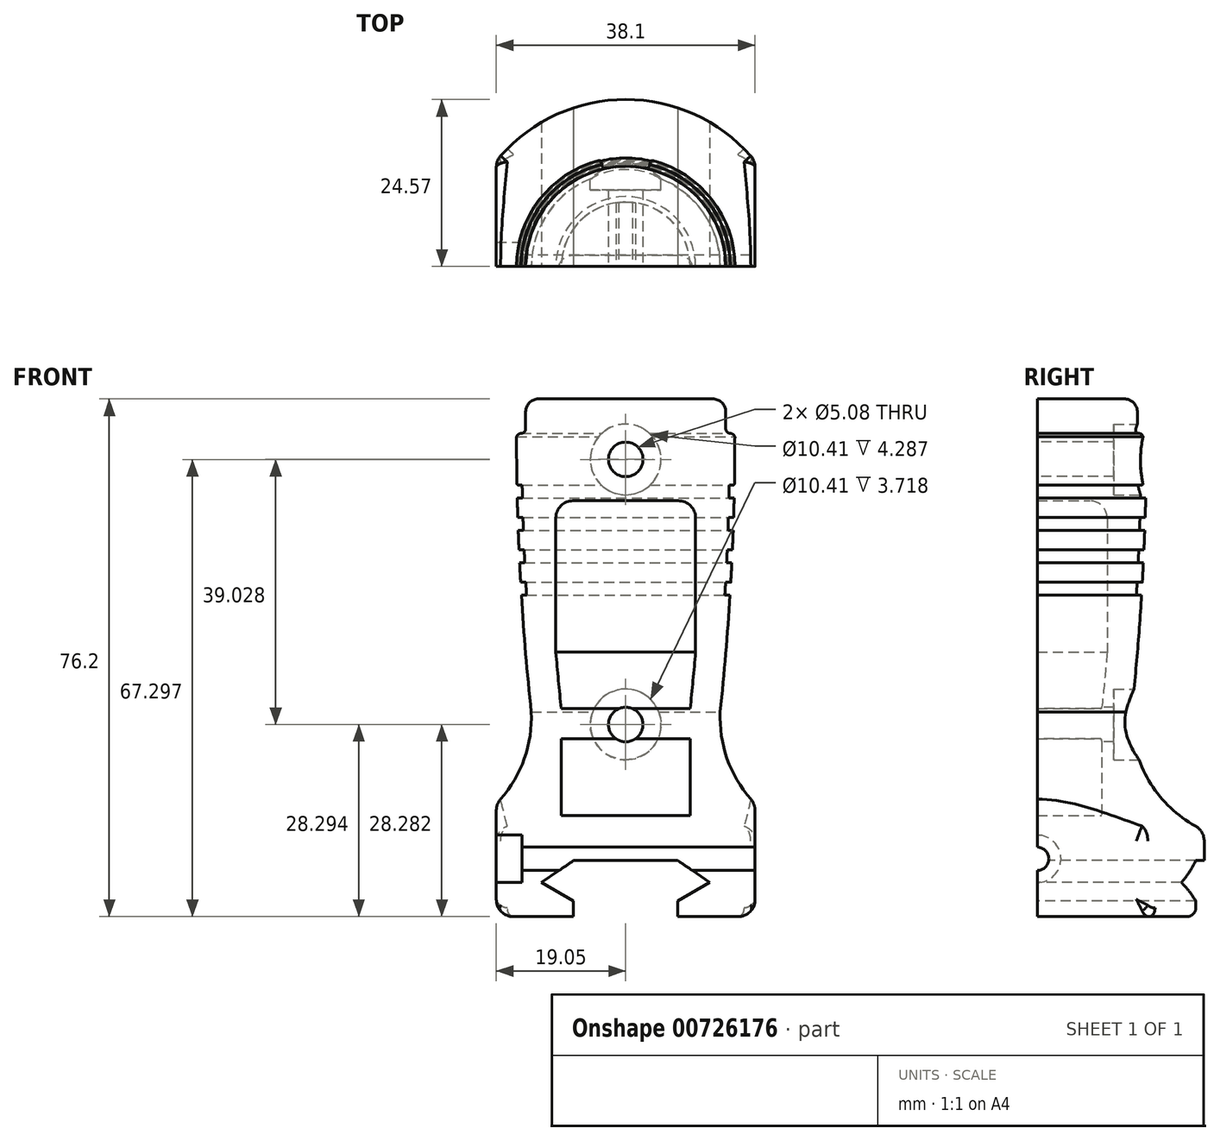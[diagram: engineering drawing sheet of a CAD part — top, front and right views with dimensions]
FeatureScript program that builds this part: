
annotation { "Feature Type Name" : "Feature", "Feature Type Description" : "" }
export const myFeature = defineFeature(function(context is Context, id is Id, definition is map)
    precondition{}
    {
        {
            var Q0;
            Q0=qCreatedBy(makeId("Front.planeOp"),FACE);
            var sketch = newSketch(context, id + "F0", { "sketchPlane" : qUnion([Q0])});
            skLineSegment(sketch, "E0", {"start": v(0, 76.2) * mm, "end": v(12.83, 76.2) * mm});
            skLineSegment(sketch, "E1.0", {"start": v(15.4, 71.12) * mm, "end": v(15.43, 71.12) * mm});
            skLineSegment(sketch, "E2.0", {"start": v(14.73, 71.82) * mm, "end": v(14.73, 74.3) * mm});
            skPoint(sketch, "E3.visualSharp", {"position": v(16.2, 71.12) * mm});
            skArc(sketch, "E3.filletArc", {"start": v(16.07, 70.62) * mm, "mid": v(15.82, 70.98) * mm, "end": v(15.4, 71.12) * mm});
            skPoint(sketch, "E4.visualSharp", {"position": v(14.73, 71.12) * mm});
            skArc(sketch, "E4.filletArc", {"start": v(14.73, 71.82) * mm, "mid": v(14.94, 71.32) * mm, "end": v(15.43, 71.12) * mm});
            skPoint(sketch, "E5.visualSharp", {"position": v(14.73, 76.2) * mm});
            skArc(sketch, "E5.filletArc", {"start": v(14.73, 74.3) * mm, "mid": v(14.17, 75.64) * mm, "end": v(12.83, 76.2) * mm});
            skArc(sketch, "E6", {"start": v(13.9, 30.14) * mm, "mid": v(14.73, 38.71) * mm, "end": v(15.36, 47.3) * mm});
            skPoint(sketch, "E7.orphan", {"position": v(16.2, 0) * mm});
            skLineSegment(sketch, "E8.0", {"start": v(15.24, 63.5) * mm, "end": v(15.76, 63.5) * mm});
            skLineSegment(sketch, "E9.0", {"start": v(15.2, 61.6) * mm, "end": v(15.97, 61.6) * mm});
            skLineSegment(sketch, "E10.0", {"start": v(15.12, 58.74) * mm, "end": v(15.89, 58.74) * mm});
            skLineSegment(sketch, "E11.0", {"start": v(15.06, 56.83) * mm, "end": v(15.82, 56.83) * mm});
            skLineSegment(sketch, "E12.0", {"start": v(14.94, 53.98) * mm, "end": v(15.7, 53.98) * mm});
            skLineSegment(sketch, "E13.0", {"start": v(14.86, 52.07) * mm, "end": v(15.62, 52.07) * mm});
            skLineSegment(sketch, "E14.0", {"start": v(14.7, 49.21) * mm, "end": v(15.47, 49.21) * mm});
            skLineSegment(sketch, "E15.0", {"start": v(14.6, 47.3) * mm, "end": v(15.36, 47.3) * mm});
            skArc(sketch, "E16.0", {"start": v(14.6, 47.3) * mm, "mid": v(14.65, 48.26) * mm, "end": v(14.7, 49.21) * mm});
            skArc(sketch, "E17.trimOffspring", {"start": v(16.01, 63.75) * mm, "mid": v(16.06, 67.18) * mm, "end": v(16.07, 70.62) * mm});
            skArc(sketch, "E18.trimOffspring", {"start": v(15.2, 61.6) * mm, "mid": v(15.22, 62.55) * mm, "end": v(15.24, 63.5) * mm});
            skArc(sketch, "E19.trimOffspring", {"start": v(15.89, 58.74) * mm, "mid": v(15.93, 60.17) * mm, "end": v(15.97, 61.6) * mm});
            skArc(sketch, "E20.trimOffspring", {"start": v(15.06, 56.83) * mm, "mid": v(15.1, 57.78) * mm, "end": v(15.12, 58.74) * mm});
            skArc(sketch, "E21.trimOffspring", {"start": v(15.7, 53.98) * mm, "mid": v(15.77, 55.4) * mm, "end": v(15.82, 56.83) * mm});
            skArc(sketch, "E22.trimOffspring", {"start": v(14.86, 52.07) * mm, "mid": v(14.9, 53.02) * mm, "end": v(14.94, 53.98) * mm});
            skArc(sketch, "E23.trimOffspring", {"start": v(15.47, 49.21) * mm, "mid": v(15.55, 50.64) * mm, "end": v(15.62, 52.07) * mm});
            skPoint(sketch, "E24.visualSharp", {"position": v(16, 63.5) * mm});
            skArc(sketch, "E24.filletArc", {"start": v(15.76, 63.5) * mm, "mid": v(15.93, 63.57) * mm, "end": v(16.01, 63.75) * mm});
            skLineSegment(sketch, "E25", {"start": v(0, 0) * mm, "end": v(23.3, 0) * mm});
            skLineSegment(sketch, "E26", {"start": v(24.57, 1.27) * mm, "end": v(24.57, 11.14) * mm});
            skArc(sketch, "E27", {"start": v(13.9, 30.14) * mm, "mid": v(16.2, 20.42) * mm, "end": v(23.27, 13.36) * mm});
            skPoint(sketch, "E28.visualSharp", {"position": v(24.57, 12.7) * mm});
            skArc(sketch, "E28.filletArc", {"start": v(24.57, 11.14) * mm, "mid": v(24.22, 12.43) * mm, "end": v(23.27, 13.36) * mm});
            skPoint(sketch, "E29.visualSharp", {"position": v(24.57, 0) * mm});
            skArc(sketch, "E29.filletArc", {"start": v(23.3, 0) * mm, "mid": v(24.2, 0.37) * mm, "end": v(24.57, 1.27) * mm});
            skLineSegment(sketch, "E30.0", {"start": v(10.29, 38.93) * mm, "end": v(10.29, 58.67) * mm});
            skArc(sketch, "E31.0", {"start": v(9.49, 30.6) * mm, "mid": v(9.91, 34.77) * mm, "end": v(10.29, 38.93) * mm});
            skLineSegment(sketch, "E32", {"start": v(9.49, 30.6) * mm, "end": v(0, 30.6) * mm});
            skLineSegment(sketch, "E33.0", {"start": v(9.49, 26.16) * mm, "end": v(0, 26.16) * mm});
            skLineSegment(sketch, "E34", {"start": v(9.49, 26.16) * mm, "end": v(9.49, 14.86) * mm});
            skLineSegment(sketch, "E35", {"start": v(9.49, 14.86) * mm, "end": v(0, 14.86) * mm});
            skLineSegment(sketch, "E36.trimOffspring", {"start": v(0, 26.16) * mm, "end": v(0, 30.6) * mm});
            skLineSegment(sketch, "E37.trimOffspring", {"start": v(0, 61.21) * mm, "end": v(0, 76.2) * mm});
            skLineSegment(sketch, "E38", {"start": v(0, 14.86) * mm, "end": v(0, 0) * mm});
            skLineSegment(sketch, "E39.0", {"start": v(0, 61.21) * mm, "end": v(7.75, 61.21) * mm});
            skPoint(sketch, "E40.visualSharp", {"position": v(10.29, 61.21) * mm});
            skArc(sketch, "E40.filletArc", {"start": v(10.29, 58.67) * mm, "mid": v(9.54, 60.47) * mm, "end": v(7.75, 61.21) * mm});
            skSolve(sketch);
        }
        {
            var Q0;
            Q0=makeQuery(id+"F0.imprint","IMPRINT",FACE,{"disambiguationData":[TD([[makeQuery(id+"F0.imprint","IMPRINT",EDGE,{"derivedFrom":sQuery(id+"F0.wireOp",EDGE,"E0")}),-1.0]])]});
            var Q1;
            Q1=sQuery(id+"F0.wireOp",EDGE,"E37.trimOffspring");
            revolve(context, id + "F1", {"surfaceOperationType" : NewSurfaceOperationType.NEW, "entities" : qUnion([Q0]), "axis" : qUnion([Q1]), "revolveType" : RevolveType.FULL});
        }
        {
            var Q0;
            Q0=qCreatedBy(makeId("Front.planeOp"),FACE);
            var sketch = newSketch(context, id + "F2", { "sketchPlane" : qUnion([Q0])});
            skLineSegment(sketch, "E41.0", {"start": v(19.05, 0) * mm, "end": v(19.05, 22.93) * mm});
            skLineSegment(sketch, "E42.0", {"start": v(-19.05, 0) * mm, "end": v(-19.05, 22.93) * mm});
            skLineSegment(sketch, "E43", {"start": v(0, 0) * mm, "end": v(0, 22.93) * mm});
            skLineSegment(sketch, "E44.0", {"start": v(7.68, 0) * mm, "end": v(7.68, 2.29) * mm});
            skLineSegment(sketch, "E45", {"start": v(7.68, 0) * mm, "end": v(19.05, 0) * mm});
            skLineSegment(sketch, "E46.0", {"start": v(0, 8.26) * mm, "end": v(7.68, 8.26) * mm});
            skLineSegment(sketch, "E47", {"start": v(7.68, 2.29) * mm, "end": v(12.38, 5.02) * mm});
            skLineSegment(sketch, "E48", {"start": v(12.38, 5.02) * mm, "end": v(7.68, 8.26) * mm});
            skLineSegment(sketch, "E49.MirrorCS", {"start": v(0, 8.26) * mm, "end": v(-7.68, 8.26) * mm});
            skLineSegment(sketch, "E50.MirrorCS", {"start": v(-12.38, 5.02) * mm, "end": v(-7.68, 8.26) * mm});
            skLineSegment(sketch, "E51.MirrorCS", {"start": v(-7.68, 2.29) * mm, "end": v(-12.38, 5.02) * mm});
            skLineSegment(sketch, "E52.MirrorCS", {"start": v(-7.68, 0) * mm, "end": v(-7.68, 2.29) * mm});
            skPoint(sketch, "E53.orphan", {"position": v(7.68, 5.02) * mm});
            skPoint(sketch, "E54.orphan", {"position": v(-7.68, 5.02) * mm});
            skLineSegment(sketch, "E55", {"start": v(-7.68, 0) * mm, "end": v(-19.05, 0) * mm});
            skLineSegment(sketch, "E56", {"start": v(-19.05, 22.93) * mm, "end": v(-34.37, 22.93) * mm});
            skLineSegment(sketch, "E57", {"start": v(-34.37, 22.93) * mm, "end": v(-34.37, -12.19) * mm});
            skLineSegment(sketch, "E58", {"start": v(-34.37, -12.19) * mm, "end": v(36.04, -12.19) * mm});
            skLineSegment(sketch, "E59", {"start": v(36.04, -12.19) * mm, "end": v(36.04, 22.93) * mm});
            skLineSegment(sketch, "E60", {"start": v(36.04, 22.93) * mm, "end": v(19.05, 22.93) * mm});
            skSolve(sketch);
        }
        {
            var Q0;
            Q0=makeQuery(id+"F2.imprint","IMPRINT",FACE,{"disambiguationData":[TD([[makeQuery(id+"F2.imprint","IMPRINT",EDGE,{"derivedFrom":sQuery(id+"F2.wireOp",EDGE,"E41.0")}),-1.0]])]});
            extrude(context, id + "F3", {"entities" : qUnion([Q0]), "operationType" : NewBodyOperationType.REMOVE, "endBound" : BoundingType.SYMMETRIC, "oppositeDirection" : true, "depth" : 50.8 * mm, "offsetDistance" : 25.4 * mm});
        }
        {
            var Q0;
            Q0=makeQuery(id+"F3.boolean.opBoolean","INTERSECT",EDGE,{"derivedFrom":[makeQuery(id+"F1.opRevolve","SWEPT_FACE",FACE,{"disambiguationData":[OSD([sQuery(id+"F0.wireOp",EDGE,"E27")])]}),makeQuery(id+"F3.opExtrude","SWEPT_FACE",FACE,{"disambiguationData":[OSD([sQuery(id+"F2.wireOp",EDGE,"E41.0")])]})]});
            var Q1;
            Q1=makeQuery(id+"F3.boolean.opBoolean","INTERSECT",EDGE,{"derivedFrom":[makeQuery(id+"F1.opRevolve","SWEPT_FACE",FACE,{"disambiguationData":[OSD([sQuery(id+"F0.wireOp",EDGE,"E27")])]}),makeQuery(id+"F3.opExtrude","SWEPT_FACE",FACE,{"disambiguationData":[OSD([sQuery(id+"F2.wireOp",EDGE,"E42.0")])]})]});
            var Q2;
            Q2=makeQuery(id+"F3.boolean.opBoolean","INTERSECT",EDGE,{"disambiguationData":[OD(0.0)],"derivedFrom":[makeQuery(id+"F1.opRevolve","SWEPT_FACE",FACE,{"disambiguationData":[OSD([sQuery(id+"F0.wireOp",EDGE,"E26")])]}),makeQuery(id+"F3.opExtrude","SWEPT_FACE",FACE,{"disambiguationData":[OSD([sQuery(id+"F2.wireOp",EDGE,"E42.0")])]})]});
            fillet(context, id + "F4", {"entities" : qUnion([Q0, Q1, Q2]), "radius" : 2.54 * mm, "tangentPropagation" : true, "allowEdgeOverflow" : false});
        }
        {
            var Q0;
            Q0=qCreatedBy(makeId("Right.planeOp"),FACE);
            var sketch = newSketch(context, id + "F5", { "sketchPlane" : qUnion([Q0])});
            skCircle(sketch, "E61", {"center": v(0, 8.5) * mm, "radius": 1.71 * mm});
            skSolve(sketch);
        }
        {
            var Q0;
            Q0=qSketchRegion(id+"F5",true);
            extrude(context, id + "F6", {"entities" : qUnion([Q0]), "operationType" : NewBodyOperationType.REMOVE, "endBound" : BoundingType.SYMMETRIC, "oppositeDirection" : true, "depth" : 76.2 * mm, "offsetDistance" : 25.4 * mm});
        }
        {
            var Q0;
            Q0=makeQuery(id+"F3.boolean.opBoolean","COPY",FACE,{"derivedFrom":makeQuery(id+"F3.opExtrude","SWEPT_FACE",FACE,{"disambiguationData":[OSD([sQuery(id+"F2.wireOp",EDGE,"E42.0")])]})});
            var sketch = newSketch(context, id + "F7", { "sketchPlane" : qUnion([Q0])});
            skCircle(sketch, "E62", {"center": v(0, 8.5) * mm, "radius": 3.5 * mm});
            skSolve(sketch);
        }
        {
            var Q0;
            Q0=qSketchRegion(id+"F7",true);
            extrude(context, id + "F8", {"entities" : qUnion([Q0]), "operationType" : NewBodyOperationType.REMOVE, "oppositeDirection" : true, "depth" : 3.8 * mm, "offsetDistance" : 25.4 * mm});
        }
        {
            var Q0;
            Q0=qCreatedBy(makeId("Front.planeOp"),FACE);
            var sketch = newSketch(context, id + "F9", { "sketchPlane" : qUnion([Q0])});
            skCircle(sketch, "E63", {"center": v(0, 67.31) * mm, "radius": 2.54 * mm});
            skCircle(sketch, "E64", {"center": v(0, 28.28) * mm, "radius": 2.54 * mm});
            skSolve(sketch);
        }
        {
            var Q0;
            Q0 = qSketchRegion(id + "F9", true);
            extrude(context, id + "F10", {"entities" : qUnion([Q0]), "operationType" : NewBodyOperationType.REMOVE, "endBound" : BoundingType.SYMMETRIC, "oppositeDirection" : true, "depth" : 76.2 * mm, "offsetDistance" : 25.4 * mm});
        }
        {
            var Q0;
            Q0=makeQuery(id+"F3.boolean.opBoolean","INTERSECT",VERTEX,{"disambiguationData":[OD(1.0)],"derivedFrom":[makeQuery(id+"F1.opRevolve","SWEPT_FACE",FACE,{"disambiguationData":[OSD([sQuery(id+"F0.wireOp",EDGE,"E26")])]}),makeQuery(id+"F3.opExtrude","SWEPT_FACE",FACE,{"disambiguationData":[OSD([sQuery(id+"F2.wireOp",EDGE,"E51.MirrorCS")])]}),makeQuery(id+"F3.opExtrude","SWEPT_FACE",FACE,{"disambiguationData":[OSD([sQuery(id+"F2.wireOp",EDGE,"E52.MirrorCS")])]})]});
            var Q1;
            Q1=makeQuery(id+"F3.boolean.opBoolean","INTERSECT",VERTEX,{"disambiguationData":[OD(1.0)],"derivedFrom":[makeQuery(id+"F1.opRevolve","SWEPT_FACE",FACE,{"disambiguationData":[OSD([sQuery(id+"F0.wireOp",EDGE,"E26")])]}),makeQuery(id+"F3.opExtrude","SWEPT_FACE",FACE,{"disambiguationData":[OSD([sQuery(id+"F2.wireOp",EDGE,"E46.0"),sQuery(id+"F2.wireOp",EDGE,"E49.MirrorCS")])]}),makeQuery(id+"F3.opExtrude","SWEPT_FACE",FACE,{"disambiguationData":[OSD([sQuery(id+"F2.wireOp",EDGE,"E50.MirrorCS")])]})]});
            var Q2;
            Q2=makeQuery(id+"F3.boolean.opBoolean","INTERSECT",VERTEX,{"disambiguationData":[OD(1.0)],"derivedFrom":[makeQuery(id+"F1.opRevolve","SWEPT_FACE",FACE,{"disambiguationData":[OSD([sQuery(id+"F0.wireOp",EDGE,"E26")])]}),makeQuery(id+"F3.opExtrude","SWEPT_FACE",FACE,{"disambiguationData":[OSD([sQuery(id+"F2.wireOp",EDGE,"E46.0"),sQuery(id+"F2.wireOp",EDGE,"E49.MirrorCS")])]}),makeQuery(id+"F3.opExtrude","SWEPT_FACE",FACE,{"disambiguationData":[OSD([sQuery(id+"F2.wireOp",EDGE,"E48")])]})]});
            cPlane(context, id + "F11", {"entities" : qUnion([Q0, Q1, Q2]), "cplaneType" : CPlaneType.THREE_POINT, "offset" : 25.4 * mm, "width" : 152.4 * mm, "height" : 152.4 * mm});
        }
        {
            var Q0;
            Q0=qCreatedBy(id+"F11.planeOp",FACE);
            var sketch = newSketch(context, id + "F12", { "sketchPlane" : qUnion([Q0])});
            skCircle(sketch, "E65", {"center": v(0, 28.3) * mm, "radius": 5.2 * mm});
            skCircle(sketch, "E66", {"center": v(0, 67.3) * mm, "radius": 5.2 * mm});
            skSolve(sketch);
        }
        {
            var Q0;
            Q0 = qSketchRegion(id + "F12", true);
            extrude(context, id + "F13", {"entities" : qUnion([Q0]), "operationType" : NewBodyOperationType.REMOVE, "depth" : 12.06 * mm, "offsetDistance" : 25.4 * mm});
        }
        {
            var Q0;
            Q0=qCreatedBy(makeId("Right.planeOp"),FACE);
            var sketch = newSketch(context, id + "F14", { "sketchPlane" : qUnion([Q0])});
            skLineSegment(sketch, "E67", {"start": v(0, 0) * mm, "end": v(0, 80.14) * mm});
            skLineSegment(sketch, "E68", {"start": v(0, 80.14) * mm, "end": v(-48.46, 80.14) * mm});
            skLineSegment(sketch, "E69", {"start": v(-48.46, 80.14) * mm, "end": v(-48.46, 0) * mm});
            skLineSegment(sketch, "E70", {"start": v(-48.46, 0) * mm, "end": v(0, 0) * mm});
            skSolve(sketch);
        }
        {
            var Q0;
            Q0 = qSketchRegion(id + "F14", true);
            extrude(context, id + "F15", {"entities" : qUnion([Q0]), "operationType" : NewBodyOperationType.REMOVE, "endBound" : BoundingType.SYMMETRIC, "oppositeDirection" : true, "depth" : 76.2 * mm, "offsetDistance" : 25.4 * mm});
        }
    });
